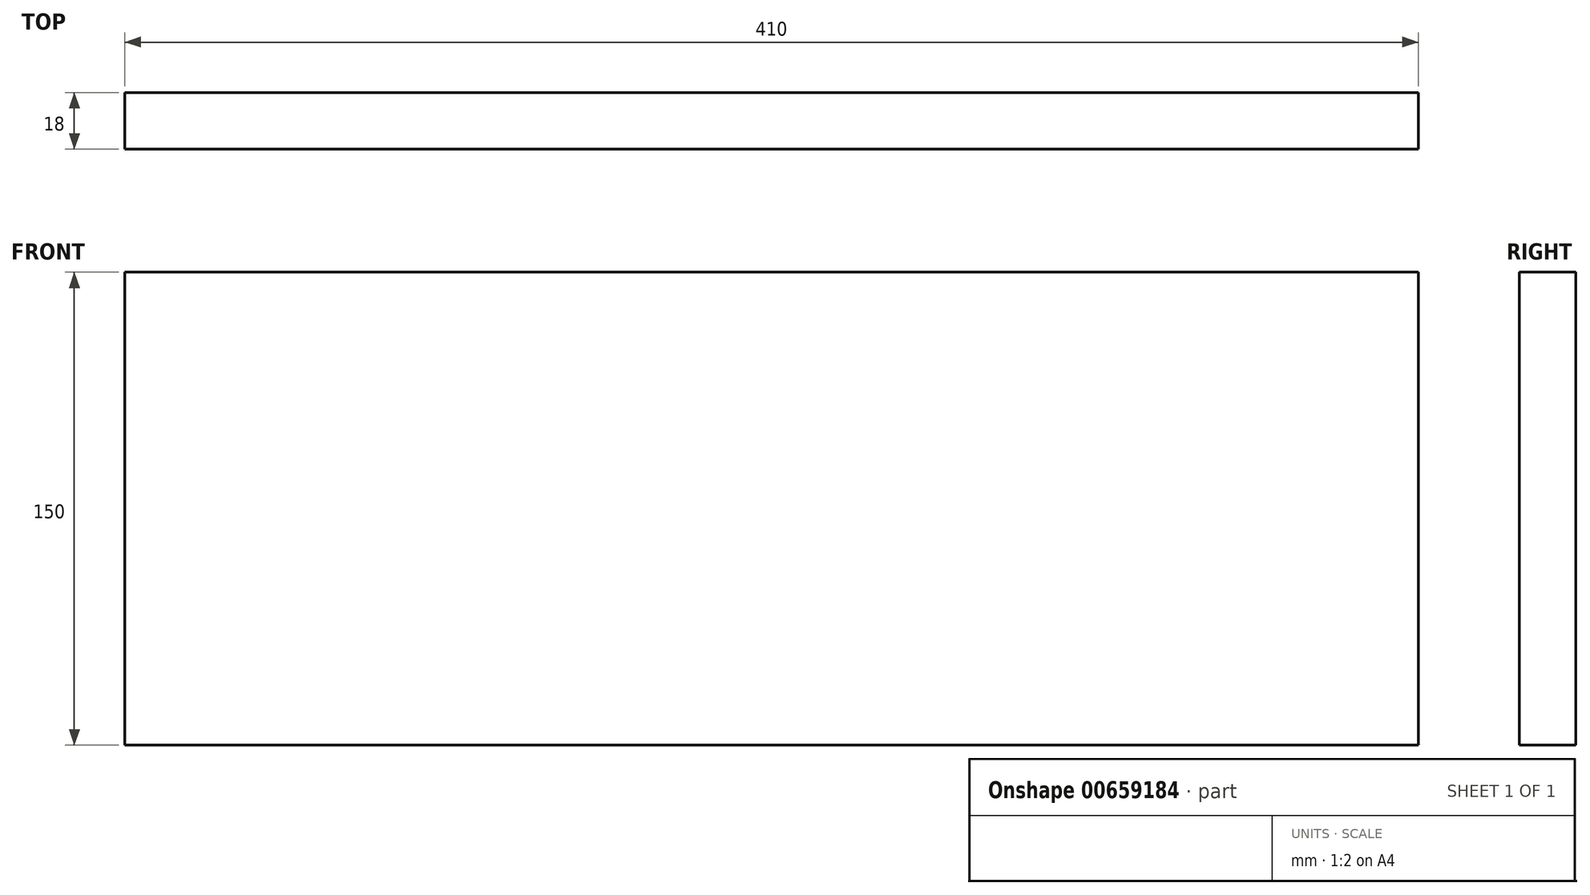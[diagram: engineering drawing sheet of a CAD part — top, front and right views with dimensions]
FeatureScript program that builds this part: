
annotation { "Feature Type Name" : "Feature", "Feature Type Description" : "" }
export const myFeature = defineFeature(function(context is Context, id is Id, definition is map)
    precondition{}
    {
        {
            var Q0;
            Q0=qCreatedBy(makeId("Front.planeOp"),FACE);
            var sketch = newSketch(context, id + "F0", { "sketchPlane" : qUnion([Q0])});
            skLineSegment(sketch, "E0.bottom", {"start": v(-205, -75) * mm, "end": v(205, -75) * mm});
            skLineSegment(sketch, "E0.top", {"start": v(-205, 75) * mm, "end": v(205, 75) * mm});
            skLineSegment(sketch, "E0.left", {"start": v(-205, -75) * mm, "end": v(-205, 75) * mm});
            skLineSegment(sketch, "E0.right", {"start": v(205, -75) * mm, "end": v(205, 75) * mm});
            skPoint(sketch, "E0.middle", {"position": v(0, 0) * mm});
            skSolve(sketch);
        }
        {
            var Q0;
            Q0=makeQuery(id+"F0.imprint","IMPRINT",FACE,{"disambiguationData":[TD([[makeQuery(id+"F0.imprint","IMPRINT",EDGE,{"derivedFrom":sQuery(id+"F0.wireOp",EDGE,"E0.bottom")}),1.0]])]});
            extrude(context, id + "F1", {"entities" : qUnion([Q0]), "endBound" : BoundingType.SYMMETRIC, "depth" : 18 * mm, "offsetDistance" : 25 * mm});
        }
    });
